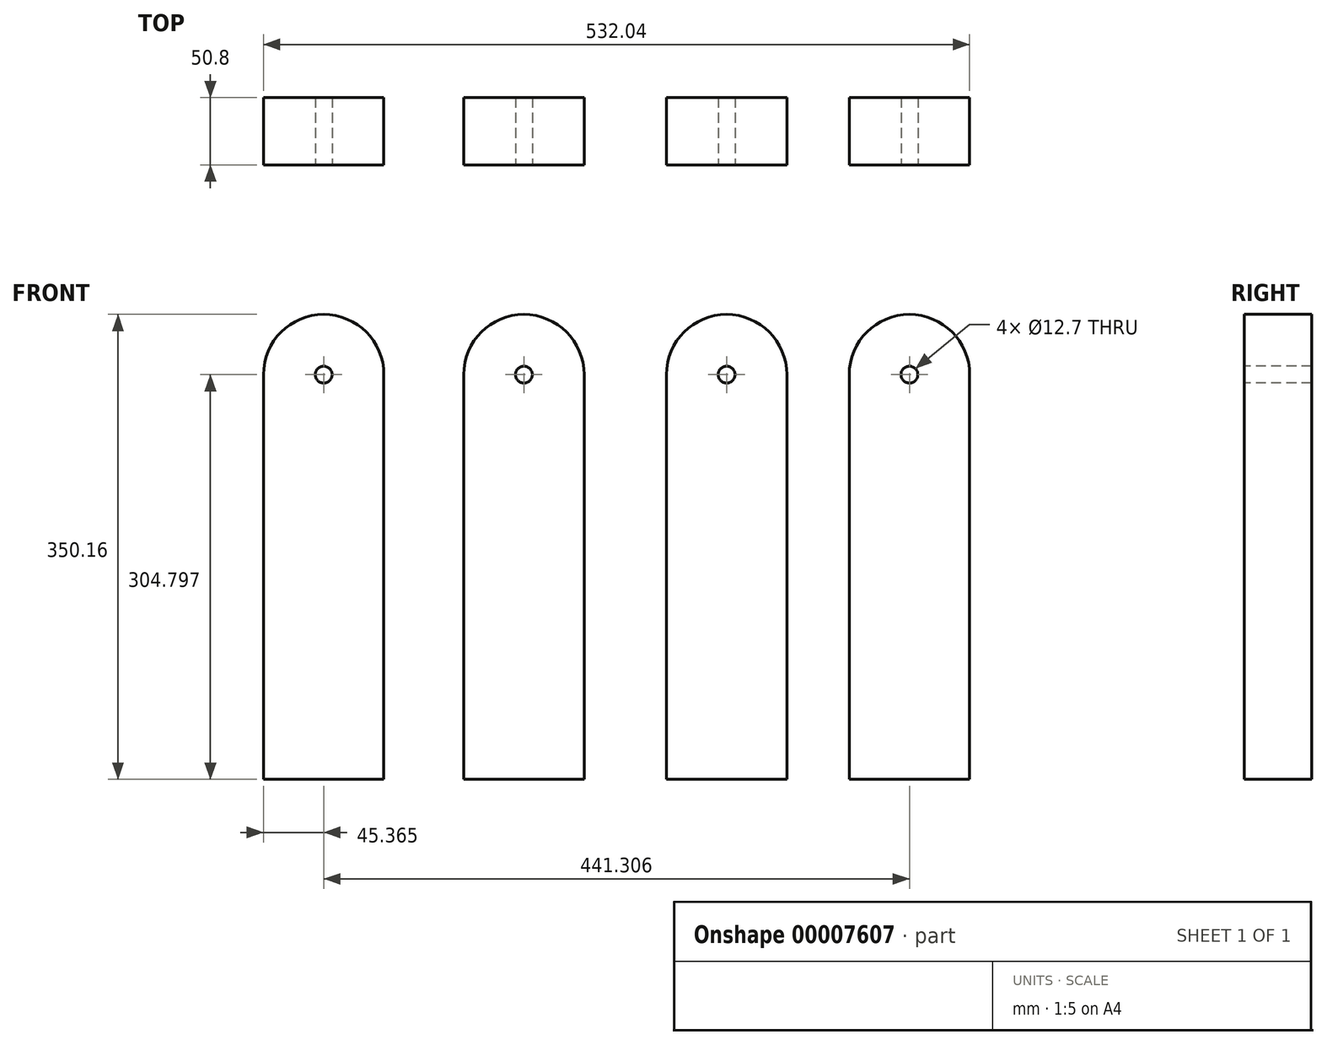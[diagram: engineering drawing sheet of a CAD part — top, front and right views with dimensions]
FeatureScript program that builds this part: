
annotation { "Feature Type Name" : "Feature", "Feature Type Description" : "" }
export const myFeature = defineFeature(function(context is Context, id is Id, definition is map)
    precondition{}
    {
        {
            var Q0;
            Q0=qCreatedBy(makeId("Front.planeOp"),FACE);
            var sketch = newSketch(context, id + "F0", { "sketchPlane" : qUnion([Q0])});
            skLineSegment(sketch, "E0.bottom", {"start": v(1.66, 144.2) * mm, "end": v(-89.07, 144.2) * mm});
            skLineSegment(sketch, "E0.top", {"start": v(1.66, -160.6) * mm, "end": v(-89.07, -160.6) * mm});
            skLineSegment(sketch, "E0.left", {"start": v(1.66, 144.2) * mm, "end": v(1.66, -160.6) * mm});
            skLineSegment(sketch, "E0.right", {"start": v(-89.07, 144.2) * mm, "end": v(-89.07, -160.6) * mm});
            skArc(sketch, "E1", {"start": v(1.66, 144.2) * mm, "mid": v(-43.7, 189.57) * mm, "end": v(-89.07, 144.2) * mm});
            skSolve(sketch);
        }
        {
            var Q0;
            Q0=makeQuery(id+"F0.imprint","IMPRINT",FACE,{"disambiguationData":[TD([[makeQuery(id+"F0.imprint","IMPRINT",EDGE,{"derivedFrom":sQuery(id+"F0.wireOp",EDGE,"E0.bottom")}),1.0]])]});
            var Q1;
            Q1=makeQuery(id+"F0.imprint","IMPRINT",FACE,{"disambiguationData":[TD([[makeQuery(id+"F0.imprint","IMPRINT",EDGE,{"derivedFrom":sQuery(id+"F0.wireOp",EDGE,"E0.bottom")}),-1.0]])]});
            extrude(context, id + "F1", {"entities" : qUnion([Q0, Q1]), "depth" : 50.8 * mm});
        }
        {
            var Q0;
            Q0=makeQuery(id+"F1.opExtrude","CAP_FACE",FACE,{"disambiguationData":[OSD([sQuery(id+"F0.wireOp",EDGE,"E0.top"),sQuery(id+"F0.wireOp",EDGE,"E0.left"),sQuery(id+"F0.wireOp",EDGE,"E0.right"),sQuery(id+"F0.wireOp",EDGE,"E1")])],"isStart":false});
            var sketch = newSketch(context, id + "F6", { "sketchPlane" : qUnion([Q0])});
            skLineSegment(sketch, "E2", {"start": v(-43.7, 189.57) * mm, "end": v(-43.7, -160.6) * mm, "construction": true});
            skLineSegment(sketch, "E3", {"start": v(-89.07, 144.2) * mm, "end": v(1.66, 144.2) * mm, "construction": true});
            skCircle(sketch, "E4", {"center": v(-43.7, 144.2) * mm, "radius": 6.35 * mm});
            skSolve(sketch);
        }
        {
            var Q0;
            Q0=makeQuery(id+"F6.imprint","IMPRINT",FACE,{"disambiguationData":[TD([[makeQuery(id+"F6.imprint","IMPRINT",EDGE,{"derivedFrom":sQuery(id+"F6.wireOp",EDGE,"E4")}),1.0]])]});
            extrude(context, id + "F2", {"entities" : qUnion([Q0]), "operationType" : NewBodyOperationType.REMOVE, "oppositeDirection" : true, "depth" : 93.33 * mm});
        }
        {
            var Q0;
            Q0=makeQuery(id+"F1.opExtrude","SWEPT_BODY",BODY,{"disambiguationData":[OSD([sQuery(id+"F0.wireOp",EDGE,"E0.top"),sQuery(id+"F0.wireOp",EDGE,"E0.left"),sQuery(id+"F0.wireOp",EDGE,"E0.right"),sQuery(id+"F0.wireOp",EDGE,"E1")])]});
            transform(context, id + "F3", {"entities" : qUnion([Q0]), "transformType" : TransformType.TRANSLATION_3D, "dx" : 150.87 * mm, "dy" : 0 * mm, "dz" : 0 * mm, "makeCopy" : true});
        }
        {
            var Q0;
            Q0=makeQuery(id+"F3.opPattern","COPY",BODY,{"derivedFrom":makeQuery(id+"F1.opExtrude","SWEPT_BODY",BODY,{"disambiguationData":[OSD([sQuery(id+"F0.wireOp",EDGE,"E0.top"),sQuery(id+"F0.wireOp",EDGE,"E0.left"),sQuery(id+"F0.wireOp",EDGE,"E0.right"),sQuery(id+"F0.wireOp",EDGE,"E1")])]}),"instanceName":"1"});
            transform(context, id + "F4", {"entities" : qUnion([Q0]), "transformType" : TransformType.TRANSLATION_3D, "dx" : 152.7 * mm, "dy" : 0 * mm, "dz" : 0 * mm, "makeCopy" : true});
        }
        {
            var Q0;
            Q0=makeQuery(id+"F4.opPattern","COPY",BODY,{"derivedFrom":makeQuery(id+"F3.opPattern","COPY",BODY,{"derivedFrom":makeQuery(id+"F1.opExtrude","SWEPT_BODY",BODY,{"disambiguationData":[OSD([sQuery(id+"F0.wireOp",EDGE,"E0.top"),sQuery(id+"F0.wireOp",EDGE,"E0.left"),sQuery(id+"F0.wireOp",EDGE,"E0.right"),sQuery(id+"F0.wireOp",EDGE,"E1")])]}),"instanceName":"1"}),"instanceName":"1"});
            transform(context, id + "F5", {"entities" : qUnion([Q0]), "transformType" : TransformType.TRANSLATION_3D, "dx" : 137.74 * mm, "dy" : 0 * mm, "dz" : 0 * mm, "makeCopy" : true});
        }
    });
